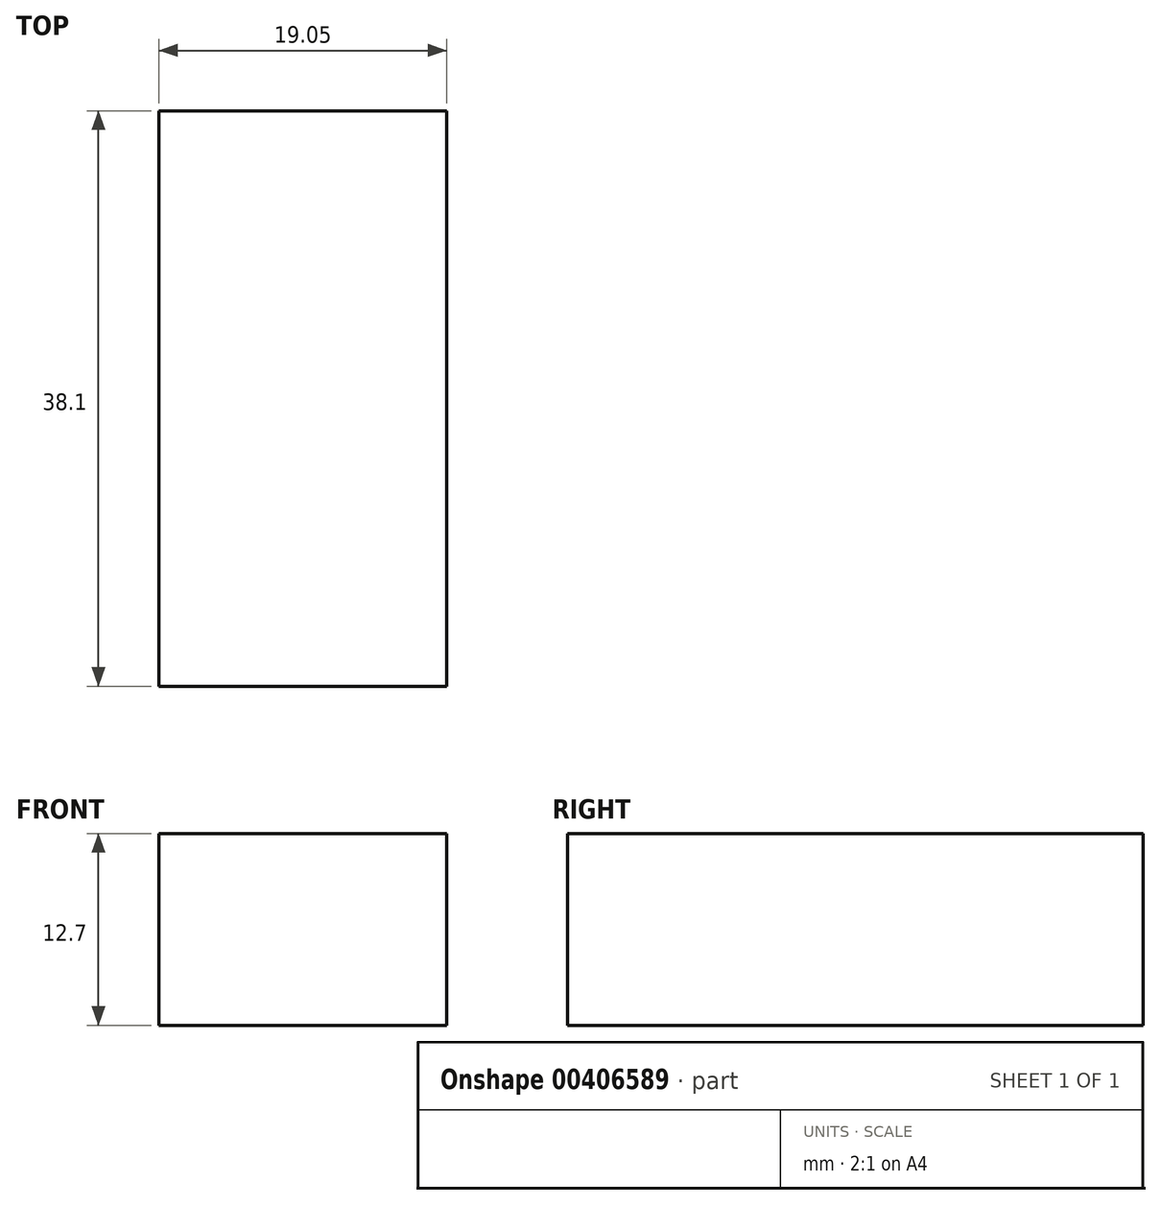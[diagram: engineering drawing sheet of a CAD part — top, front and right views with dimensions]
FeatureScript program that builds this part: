
annotation { "Feature Type Name" : "Feature", "Feature Type Description" : "" }
export const myFeature = defineFeature(function(context is Context, id is Id, definition is map)
    precondition{}
    {
        {
            var Q0;
            Q0=qCreatedBy(makeId("Front.planeOp"),FACE);
            var sketch = newSketch(context, id + "F0", { "sketchPlane" : qUnion([Q0])});
            skLineSegment(sketch, "E0.bottom", {"start": v(0, 0) * mm, "end": v(19.05, 0) * mm});
            skLineSegment(sketch, "E0.top", {"start": v(0, -12.7) * mm, "end": v(19.05, -12.7) * mm});
            skLineSegment(sketch, "E0.left", {"start": v(0, 0) * mm, "end": v(0, -12.7) * mm});
            skLineSegment(sketch, "E0.right", {"start": v(19.05, 0) * mm, "end": v(19.05, -12.7) * mm});
            skSolve(sketch);
        }
        {
            var Q0;
            Q0=makeQuery(id+"F0.imprint","IMPRINT",FACE,{"disambiguationData":[TD([[makeQuery(id+"F0.imprint","IMPRINT",EDGE,{"derivedFrom":sQuery(id+"F0.wireOp",EDGE,"E0.bottom")}),-1.0]])]});
            extrude(context, id + "F1", {"entities" : qUnion([Q0]), "depth" : 38.1 * mm});
        }
    });
